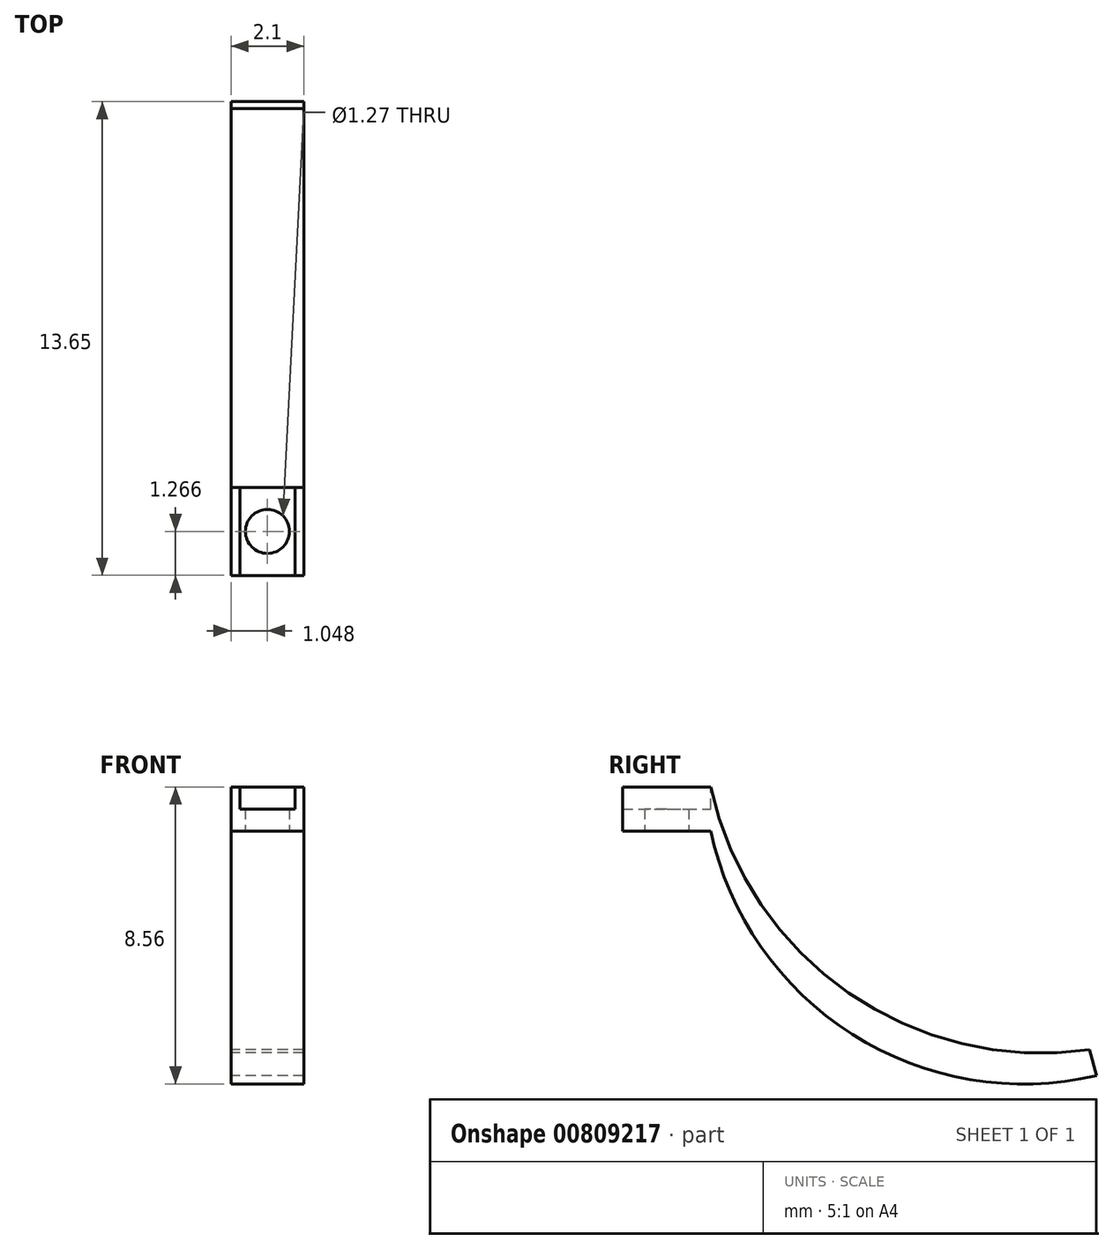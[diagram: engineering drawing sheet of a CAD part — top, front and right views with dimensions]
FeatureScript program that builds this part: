
annotation { "Feature Type Name" : "Feature", "Feature Type Description" : "" }
export const myFeature = defineFeature(function(context is Context, id is Id, definition is map)
    precondition{}
    {
        {
            var Q0;
            Q0=qCreatedBy(makeId("Right.planeOp"),FACE);
            var sketch = newSketch(context, id + "F0", { "sketchPlane" : qUnion([Q0])});
            skLineSegment(sketch, "E0.left", {"start": v(51.4, -19.58) * mm, "end": v(51.4, -18.31) * mm});
            skLineSegment(sketch, "E1.MirrorCS", {"start": v(51.4, -19.58) * mm, "end": v(53.94, -19.58) * mm});
            skLineSegment(sketch, "E2.MirrorCS", {"start": v(51.4, -18.31) * mm, "end": v(53.94, -18.31) * mm});
            skLineSegment(sketch, "E3.MirrorCS", {"start": v(63.62, -52.11) * mm, "end": v(63.62, -50.84) * mm});
            skArc(sketch, "E4", {"start": v(53.94, -18.31) * mm, "mid": v(57.9, -24.24) * mm, "end": v(64.85, -25.88) * mm});
            skArc(sketch, "E5", {"start": v(53.94, -19.58) * mm, "mid": v(58.01, -25.44) * mm, "end": v(65.05, -26.63) * mm});
            skLineSegment(sketch, "E6", {"start": v(65.05, -26.63) * mm, "end": v(64.85, -25.88) * mm});
            skSolve(sketch);
        }
        {
            var Q0;
            Q0=makeQuery(id+"F0.imprint","IMPRINT",FACE,{"disambiguationData":[TD([[makeQuery(id+"F0.imprint","IMPRINT",EDGE,{"derivedFrom":sQuery(id+"F0.wireOp",EDGE,"E0.bottom")}),-1.0]])]});
            var Q1;
            Q1=makeQuery(id+"F0.imprint","IMPRINT",FACE,{"disambiguationData":[TD([[makeQuery(id+"F0.imprint","IMPRINT",EDGE,{"derivedFrom":sQuery(id+"F0.wireOp",EDGE,"E0.right")}),1.0]])]});
            var Q2;
            Q2=makeQuery(id+"F0.imprint","IMPRINT",FACE,{"disambiguationData":[TD([[makeQuery(id+"F0.imprint","IMPRINT",EDGE,{"derivedFrom":sQuery(id+"F0.wireOp",EDGE,"E0.left")}),-1.0]])]});
            extrude(context, id + "F1", {"entities" : qUnion([Q0, Q1, Q2]), "depth" : 2.1 * mm, "offsetDistance" : 25.4 * mm});
        }
        {
            var Q0;
            Q0=makeQuery(id+"F1.opExtrude","SWEPT_FACE",FACE,{"disambiguationData":[OSD([sQuery(id+"F0.wireOp",EDGE,"E1.MirrorCS")])]});
            var sketch = newSketch(context, id + "F2", { "sketchPlane" : qUnion([Q0])});
            skLineSegment(sketch, "E7", {"start": v(0, -53.94) * mm, "end": v(0, -51.4) * mm, "construction": true});
            skLineSegment(sketch, "E8", {"start": v(0, -51.4) * mm, "end": v(2.1, -51.4) * mm, "construction": true});
            skLineSegment(sketch, "E9", {"start": v(2.1, -51.4) * mm, "end": v(2.1, -53.94) * mm, "construction": true});
            skCircle(sketch, "E10", {"center": v(1.05, -52.67) * mm, "radius": 0.64 * mm});
            skSolve(sketch);
        }
        {
            var Q0;
            Q0=makeQuery(id+"F2.imprint","IMPRINT",FACE,{"disambiguationData":[TD([[makeQuery(id+"F2.imprint","IMPRINT",EDGE,{"derivedFrom":sQuery(id+"F2.wireOp",EDGE,"E10")}),1.0]])]});
            extrude(context, id + "F3", {"entities" : qUnion([Q0]), "operationType" : NewBodyOperationType.REMOVE, "oppositeDirection" : true, "depth" : 25.4 * mm, "offsetDistance" : 25.4 * mm});
        }
        {
            var Q0;
            Q0=makeQuery(id+"F1.opExtrude","SWEPT_FACE",FACE,{"disambiguationData":[OSD([sQuery(id+"F0.wireOp",EDGE,"E2.MirrorCS")])]});
            var sketch = newSketch(context, id + "F4", { "sketchPlane" : qUnion([Q0])});
            skLineSegment(sketch, "E11", {"start": v(1.84, 51.4) * mm, "end": v(1.84, 53.94) * mm});
            skLineSegment(sketch, "E12", {"start": v(0.25, 53.94) * mm, "end": v(0.25, 51.4) * mm});
            skSolve(sketch);
        }
        {
            var Q0;
            {var subQ0=sQuery(id+"F4.wireOp",EDGE,"E11");Q0=makeQuery(id+"F4.imprint","IMPRINT",FACE,{"disambiguationData":[TD([[makeQuery(id+"F4.imprint","IMPRINT",EDGE,{"derivedFrom":subQ0}),1.0]])]});}
            extrude(context, id + "F5", {"entities" : qUnion([Q0]), "operationType" : NewBodyOperationType.REMOVE, "oppositeDirection" : true, "depth" : 0.64 * mm, "offsetDistance" : 25.4 * mm});
        }
    });
